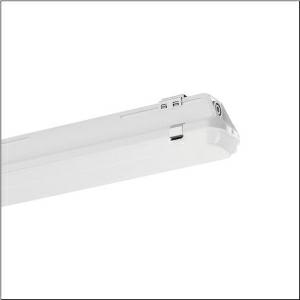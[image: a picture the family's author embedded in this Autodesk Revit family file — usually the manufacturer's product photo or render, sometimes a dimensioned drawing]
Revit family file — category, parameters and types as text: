
# Revit family: monsun_r__21_51fb30dp460b_7b4c
name_source: partatom
category: Lighting Fixtures
units: mm (PartAtom-declared; Revit-internal decimal feet)

## family parameters
Cut with Voids When Loaded = No
Host = Face
Light Source = No
Part Type = Normal
Room Calculation Point = No
Round Connector Dimension = Use Diameter
Shared = No

## types (1)
- --- (1 x LED, 5740 lm, 39.4 W, 4000K)
    Apparent Load = 39 VA
    CIE Flux Codes = 48 77 93 95 100
    Color Rendering = 80
    Color Temperature = 4000K
    Default Elevation = 1800 mm
    Description = Monsun® 21, damp-proof luminaire, chain hanger, primary optical cover: enclosure, of PA, light emission: direct distribution, primary light characteristic: symmetric, installation type: suspended mounting, surface-mounted, horizontal mounting, vertical mounting, LED, rated luminous flux: 5.740lm, luminous efficacy: 146lm/W, light colour: 840, colour temperature: 4000K, control gear: ECG DALI, with terminal, 5-pole, max. 2.5mm², mains connection: 220..240V, AC, 50/60Hz, rated input power: 39W, housing, of glass-fibre reinforced polyester, uncoated, bright grey, length: 1.590mm, width: 90mm, height: 88mm, clip for enclosure, of stainless steel (V2A), ceiling mounting element, of stainless steel (V2A), chain hanger, of stainless steel (V2A), protection rating (complete): IP66, insulation class (complete): insulation class I (protective earthing), certification: CE, ENEC, VDE, UKCA, protection symbol: D, impact resistance: IK08, permissible operating ambient temperature: -25..+35°C, standard: EN 50419, EN 60598-2-1, corresponds to IFS (International Featured Standards) requirements for safety and quality in the food industry, for indoor or canopied outdoor use, no direct snow, no direct sun, no direct rain, packaging unit: 1 piece
    Height = 89 mm
    Lamp = 1 x LED
    Lamp Light Flux = 5740 lm
    Lamp Power = 39.4 W
    Lamp count = 1
    Length = 1590 mm
    Luminous efficacy = 146 lm/W
    Manufacturer = Siteco
    ModVariant = No
    Model = 51FB30DP460B
    Mounting Place = Ceiling
    Mounting Type = Pendant
    Number of Poles = 1
    OnlyDefault = Yes
    Power Factor = 1
    Product Name = Monsun® 21
    Product group = damp-proof luminaire | ceiling pendant
    ProductGroupID = 908
    Protection Class = Protection class I
    Protection Degree = IP 66
    RLX_Detail_Level = 1
    RlxData = <blob elided: 92337 chars, md5=5ce373db>
    Socket = socket
    Standby Power = 0 W
    System Light Flux = 5740 lm
    System Power = 39 W
    Type Comments = factory setting: luminous flux: 100 % | dim-lin: 254 | 261 mA
    Type Image = l_1006717.jpg
    URL = http://relux.com
    VarID = @adj_125069
    Voltage = 0 V
    Weight = 0.00 kg
    Width = 90 mm

## geometry (parser evidence)
native form markers: Blend x4, Sweep x13
no freeform markers — native parametric forms only
